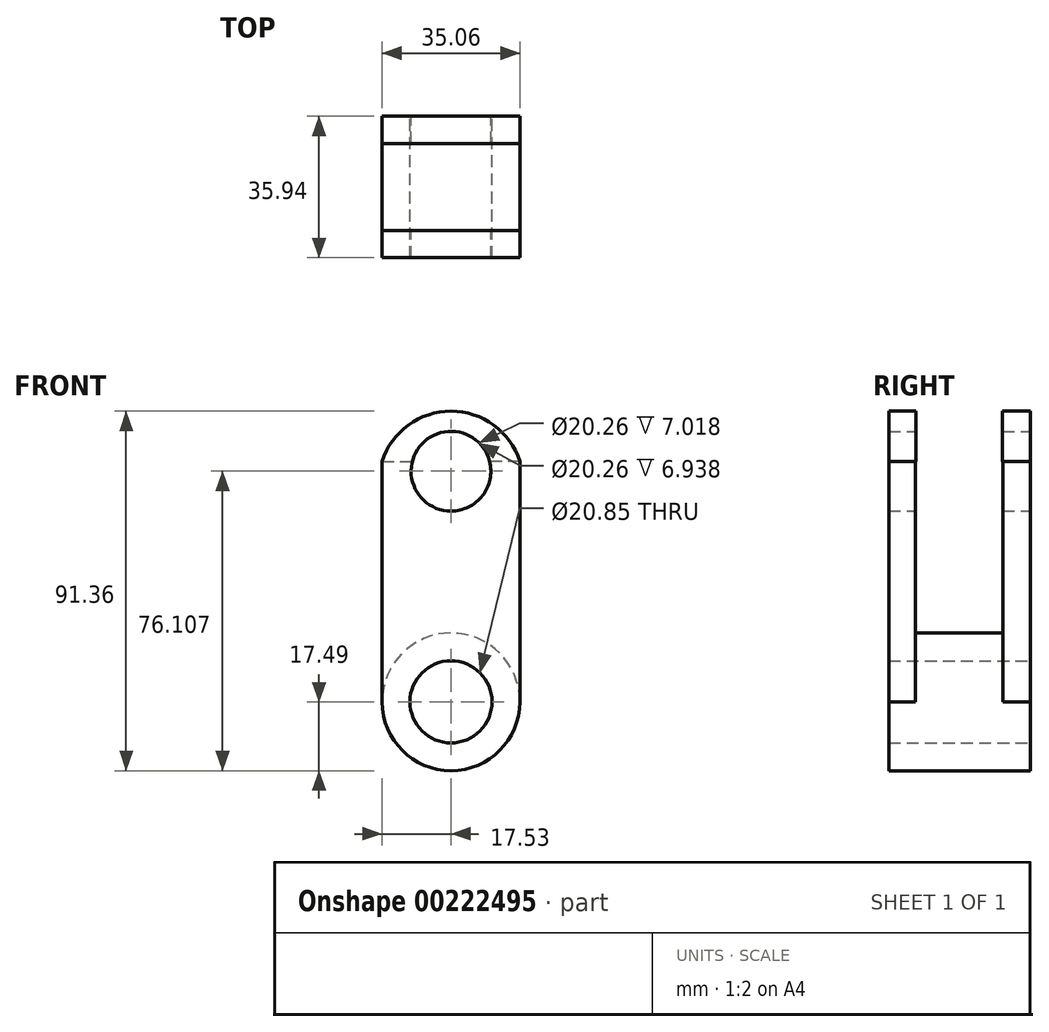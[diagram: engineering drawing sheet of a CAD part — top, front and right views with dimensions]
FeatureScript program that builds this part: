
annotation { "Feature Type Name" : "Feature", "Feature Type Description" : "" }
export const myFeature = defineFeature(function(context is Context, id is Id, definition is map)
    precondition{}
    {
        {
            var Q0;
            Q0=qCreatedBy(makeId("Front.planeOp"),FACE);
            var sketch = newSketch(context, id + "F0", { "sketchPlane" : qUnion([Q0])});
            skCircle(sketch, "E0", {"center": v(0, 0) * mm, "radius": 17.5 * mm});
            skSolve(sketch);
        }
        {
            var Q0;
            Q0=qCreatedBy(makeId("Right.planeOp"),FACE);
            var sketch = newSketch(context, id + "F1", { "sketchPlane" : qUnion([Q0])});
            skLineSegment(sketch, "E1.bottom", {"start": v(0, 0) * mm, "end": v(6.85, 0) * mm});
            skLineSegment(sketch, "E1.top", {"start": v(0, 61.13) * mm, "end": v(6.85, 61.13) * mm});
            skLineSegment(sketch, "E1.left", {"start": v(0, 0) * mm, "end": v(0, 61.13) * mm});
            skLineSegment(sketch, "E1.right", {"start": v(6.85, 0) * mm, "end": v(6.85, 61.13) * mm});
            skLineSegment(sketch, "E2.bottom", {"start": v(29, 0) * mm, "end": v(35.94, 0) * mm});
            skLineSegment(sketch, "E2.top", {"start": v(29, 61.13) * mm, "end": v(35.94, 61.13) * mm});
            skLineSegment(sketch, "E2.left", {"start": v(29, 0) * mm, "end": v(29, 61.13) * mm});
            skLineSegment(sketch, "E2.right", {"start": v(35.94, 0) * mm, "end": v(35.94, 61.13) * mm});
            skSolve(sketch);
        }
        {
            var Q0;
            Q0=makeQuery(id+"F0.imprint","IMPRINT",FACE,{"disambiguationData":[TD([[makeQuery(id+"F0.imprint","IMPRINT",EDGE,{"derivedFrom":sQuery(id+"F0.wireOp",EDGE,"E0")}),1.0]])]});
            extrude(context, id + "F2", {"entities" : qUnion([Q0]), "oppositeDirection" : true, "depth" : 35.94 * mm});
        }
        {
            var Q0;
            Q0=makeQuery(id+"F1.imprint","IMPRINT",FACE,{"disambiguationData":[TD([[makeQuery(id+"F1.imprint","IMPRINT",EDGE,{"derivedFrom":sQuery(id+"F1.wireOp",EDGE,"E2.bottom")}),1.0]])]});
            extrude(context, id + "F3", {"entities" : qUnion([Q0]), "operationType" : NewBodyOperationType.ADD, "depth" : 17.53 * mm, "hasSecondDirection" : true, "secondDirectionOppositeDirection" : true, "secondDirectionDepth" : 17.53 * mm});
        }
        {
            var Q0;
            Q0 = qSketchRegion(id + "F1", true);
            extrude(context, id + "F4", {"entities" : qUnion([Q0]), "operationType" : NewBodyOperationType.ADD, "depth" : 17.53 * mm, "hasSecondDirection" : true, "secondDirectionOppositeDirection" : true, "secondDirectionDepth" : 17.53 * mm});
        }
        {
            var Q0;
            Q0=makeQuery(id+"F4.boolean.opBoolean","MERGE",FACE,{"derivedFrom":[makeQuery(id+"F2.opExtrude","CAP_FACE",FACE,{"disambiguationData":[OSD([sQuery(id+"F0.wireOp",EDGE,"E0")])],"isStart":true}),makeQuery(id+"F4.opExtrude","SWEPT_FACE",FACE,{"disambiguationData":[OSD([sQuery(id+"F1.wireOp",EDGE,"E1.left")])]})]});
            var sketch = newSketch(context, id + "F5", { "sketchPlane" : qUnion([Q0])});
            skArc(sketch, "E3", {"start": v(17.53, 61.13) * mm, "mid": v(0, 73.87) * mm, "end": v(-17.53, 61.13) * mm});
            skSolve(sketch);
        }
        {
            var Q0;
            Q0 = qSketchRegion(id + "F5", true);
            var Q1;
            Q1=makeQuery(id+"F5.imprint","IMPRINT",FACE,{"disambiguationData":[TD([[makeQuery(id+"F5.imprint","IMPRINT",EDGE,{"derivedFrom":sQuery(id+"F5.wireOp",EDGE,"E3")}),1.0]])]});
            extrude(context, id + "F6", {"entities" : qUnion([Q0, Q1]), "operationType" : NewBodyOperationType.ADD, "oppositeDirection" : true, "depth" : 35.94 * mm});
        }
        {
            var Q0;
            Q0=qCreatedBy(makeId("Right.planeOp"),FACE);
            var sketch = newSketch(context, id + "F7", { "sketchPlane" : qUnion([Q0])});
            skLineSegment(sketch, "E4", {"start": v(6.94, 60.95) * mm, "end": v(6.94, 74.7) * mm});
            skLineSegment(sketch, "E5", {"start": v(28.92, 60.87) * mm, "end": v(28.92, 74.24) * mm});
            skLineSegment(sketch, "E6", {"start": v(28.92, 74.24) * mm, "end": v(6.94, 74.7) * mm});
            skLineSegment(sketch, "E7", {"start": v(6.94, 60.95) * mm, "end": v(28.92, 60.87) * mm});
            skSolve(sketch);
        }
        {
            var Q0;
            Q0=makeQuery(id+"F7.imprint","IMPRINT",FACE,{"disambiguationData":[TD([[makeQuery(id+"F7.imprint","IMPRINT",EDGE,{"derivedFrom":sQuery(id+"F7.wireOp",EDGE,"E4")}),-1.0]])]});
            extrude(context, id + "F8", {"entities" : qUnion([Q0]), "operationType" : NewBodyOperationType.REMOVE, "depth" : 25.4 * mm, "hasSecondDirection" : true, "secondDirectionOppositeDirection" : true, "secondDirectionDepth" : 25.4 * mm});
        }
        {
            var Q0;
            {var subQ0=sQuery(id+"F1.wireOp",EDGE,"E1.left");Q0=makeQuery(id+"F6.boolean.opBoolean","MERGE",FACE,{"derivedFrom":[makeQuery(id+"F4.boolean.opBoolean","MERGE",FACE,{"derivedFrom":[makeQuery(id+"F2.opExtrude","CAP_FACE",FACE,{"disambiguationData":[OSD([sQuery(id+"F0.wireOp",EDGE,"E0")])],"isStart":true}),makeQuery(id+"F4.opExtrude","SWEPT_FACE",FACE,{"disambiguationData":[OSD([subQ0])]})]}),makeQuery(id+"F6.opExtrude","CAP_FACE",FACE,{"disambiguationData":[OSD([sQuery(id+"F1.wireOp",EDGE,"E1.top"),subQ0,sQuery(id+"F5.wireOp",EDGE,"E3")])],"isStart":true})]});}
            var sketch = newSketch(context, id + "F9", { "sketchPlane" : qUnion([Q0])});
            skCircle(sketch, "E8", {"center": v(0, 58.62) * mm, "radius": 10.13 * mm});
            skCircle(sketch, "E9", {"center": v(0, 0) * mm, "radius": 10.43 * mm});
            skSolve(sketch);
        }
        {
            var Q0;
            Q0=makeQuery(id+"F9.imprint","IMPRINT",FACE,{"disambiguationData":[TD([[makeQuery(id+"F9.imprint","IMPRINT",EDGE,{"derivedFrom":sQuery(id+"F9.wireOp",EDGE,"E8")}),1.0]])]});
            var Q1;
            Q1=makeQuery(id+"F9.imprint","IMPRINT",FACE,{"disambiguationData":[TD([[makeQuery(id+"F9.imprint","IMPRINT",EDGE,{"derivedFrom":sQuery(id+"F9.wireOp",EDGE,"E9")}),1.0]])]});
            extrude(context, id + "F10", {"entities" : qUnion([Q0, Q1]), "operationType" : NewBodyOperationType.REMOVE, "depth" : 38.1 * mm, "hasSecondDirection" : true, "secondDirectionOppositeDirection" : true, "secondDirectionDepth" : 38.1 * mm});
        }
    });
